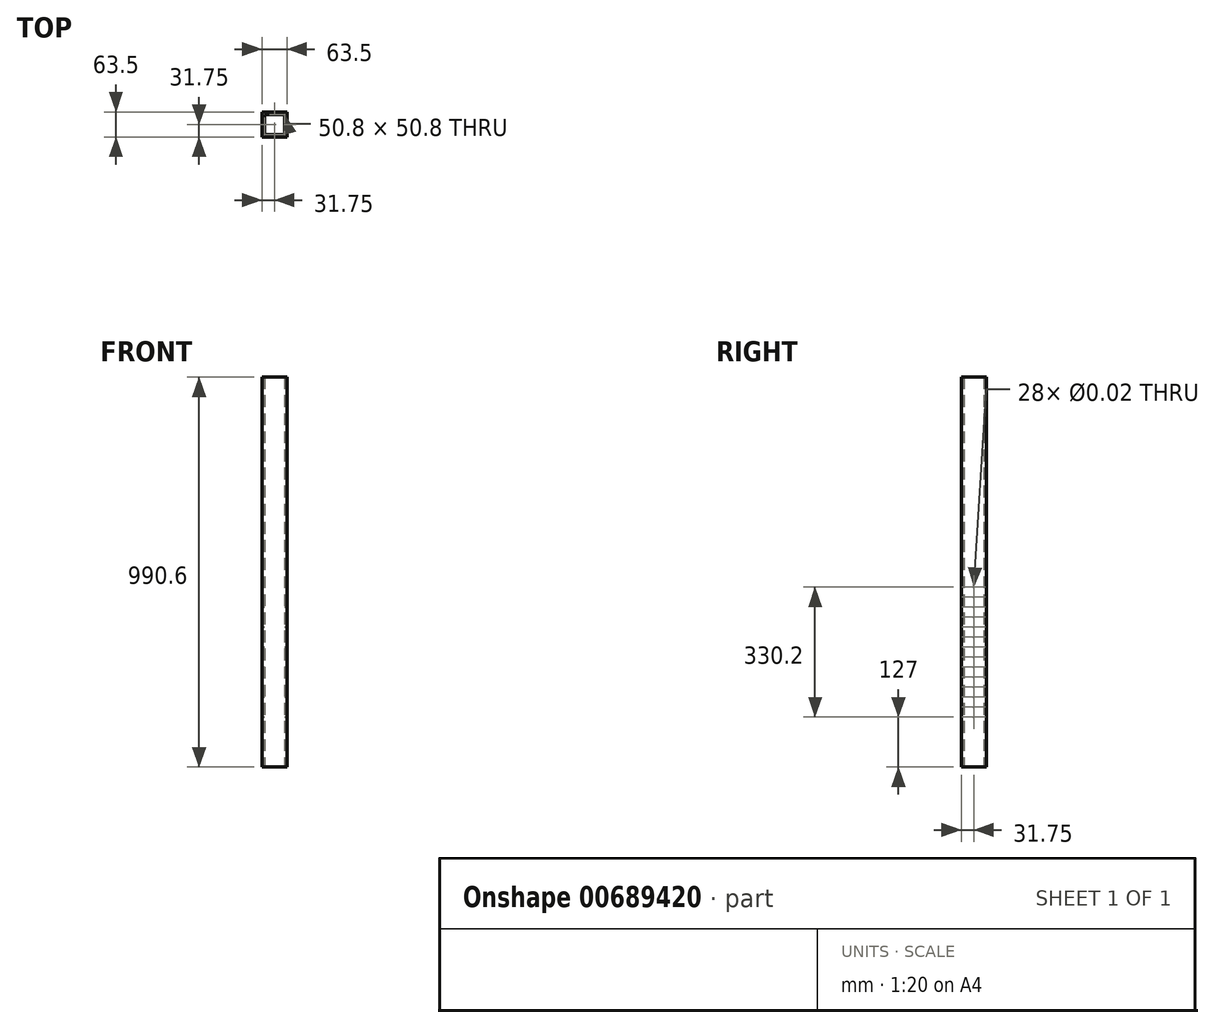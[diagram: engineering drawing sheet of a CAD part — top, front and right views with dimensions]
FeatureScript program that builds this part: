
annotation { "Feature Type Name" : "Feature", "Feature Type Description" : "" }
export const myFeature = defineFeature(function(context is Context, id is Id, definition is map)
    precondition{}
    {
        {
            var Q0;
            Q0=qCreatedBy(makeId("Top.planeOp"),FACE);
            var sketch = newSketch(context, id + "F0", { "sketchPlane" : qUnion([Q0])});
            skLineSegment(sketch, "E0.bottom", {"start": v(-31.75, 31.75) * mm, "end": v(31.75, 31.75) * mm});
            skLineSegment(sketch, "E0.top", {"start": v(-31.75, -31.75) * mm, "end": v(31.75, -31.75) * mm});
            skLineSegment(sketch, "E0.left", {"start": v(-31.75, 31.75) * mm, "end": v(-31.75, -31.75) * mm});
            skLineSegment(sketch, "E0.right", {"start": v(31.75, 31.75) * mm, "end": v(31.75, -31.75) * mm});
            skPoint(sketch, "E0.middle", {"position": v(0, 0) * mm});
            skLineSegment(sketch, "E1.bottom", {"start": v(-25.4, 25.4) * mm, "end": v(25.4, 25.4) * mm});
            skLineSegment(sketch, "E1.top", {"start": v(-25.4, -25.4) * mm, "end": v(25.4, -25.4) * mm});
            skLineSegment(sketch, "E1.left", {"start": v(-25.4, 25.4) * mm, "end": v(-25.4, -25.4) * mm});
            skLineSegment(sketch, "E1.right", {"start": v(25.4, 25.4) * mm, "end": v(25.4, -25.4) * mm});
            skSolve(sketch);
        }
        {
            var Q0;
            Q0=makeQuery(id+"F0.imprint","IMPRINT",FACE,{"disambiguationData":[TD([[makeQuery(id+"F0.imprint","IMPRINT",EDGE,{"derivedFrom":sQuery(id+"F0.wireOp",EDGE,"E0.bottom")}),-1.0]])]});
            extrude(context, id + "F1", {"entities" : qUnion([Q0]), "depth" : 990.6 * mm, "offsetDistance" : 25.4 * mm});
        }
        {
            var Q0;
            Q0=makeQuery(id+"F1.opExtrude","SWEPT_FACE",FACE,{"disambiguationData":[OSD([sQuery(id+"F0.wireOp",EDGE,"E0.right")])]});
            var sketch = newSketch(context, id + "F2", { "sketchPlane" : qUnion([Q0])});
            skPoint(sketch, "E2", {"position": v(0, 127) * mm});
            skPoint(sketch, "E3.0.1.0", {"position": v(0, 152.4) * mm});
            skPoint(sketch, "E3.0.2.0", {"position": v(0, 177.8) * mm});
            skPoint(sketch, "E3.0.3.0", {"position": v(0, 203.2) * mm});
            skPoint(sketch, "E3.0.4.0", {"position": v(0, 228.6) * mm});
            skPoint(sketch, "E3.0.5.0", {"position": v(0, 254) * mm});
            skPoint(sketch, "E3.0.6.0", {"position": v(0, 279.4) * mm});
            skPoint(sketch, "E3.0.7.0", {"position": v(0, 304.8) * mm});
            skPoint(sketch, "E3.0.8.0", {"position": v(0, 330.2) * mm});
            skPoint(sketch, "E3.0.9.0", {"position": v(0, 355.6) * mm});
            skPoint(sketch, "E3.0.10.0", {"position": v(0, 381) * mm});
            skPoint(sketch, "E3.0.11.0", {"position": v(0, 406.4) * mm});
            skPoint(sketch, "E3.0.12.0", {"position": v(0, 431.8) * mm});
            skPoint(sketch, "E3.0.13.0", {"position": v(0, 457.2) * mm});
            skLineSegment(sketch, "E3.direction1", {"start": v(0, 127) * mm, "end": v(25.4, 127) * mm, "construction": true});
            skLineSegment(sketch, "E3.direction2", {"start": v(0, 127) * mm, "end": v(0, 152.4) * mm, "construction": true});
            skSolve(sketch);
        }
        {
            var Q0;
            Q0=sQuery(id+"F2.wireOp",VERTEX,"E2");
            var Q1;
            Q1=sQuery(id+"F2.wireOp",VERTEX,"E3.0.1.0");
            var Q2;
            Q2=sQuery(id+"F2.wireOp",VERTEX,"E3.0.2.0");
            var Q3;
            Q3=sQuery(id+"F2.wireOp",VERTEX,"E3.0.3.0");
            var Q4;
            Q4=sQuery(id+"F2.wireOp",VERTEX,"E3.0.4.0");
            var Q5;
            Q5=sQuery(id+"F2.wireOp",VERTEX,"E3.0.5.0");
            var Q6;
            Q6=sQuery(id+"F2.wireOp",VERTEX,"E3.0.6.0");
            var Q7;
            Q7=sQuery(id+"F2.wireOp",VERTEX,"E3.0.7.0");
            var Q8;
            Q8=sQuery(id+"F2.wireOp",VERTEX,"E3.0.8.0");
            var Q9;
            Q9=sQuery(id+"F2.wireOp",VERTEX,"E3.0.9.0");
            var Q10;
            Q10=sQuery(id+"F2.wireOp",VERTEX,"E3.0.10.0");
            var Q11;
            Q11=sQuery(id+"F2.wireOp",VERTEX,"E3.0.11.0");
            var Q12;
            Q12=sQuery(id+"F2.wireOp",VERTEX,"E3.0.12.0");
            var Q13;
            Q13=sQuery(id+"F2.wireOp",VERTEX,"E3.0.13.0");
            var Q14;
            Q14=makeQuery(id+"F1.opExtrude","SWEPT_BODY",BODY,{"disambiguationData":[OSD([sQuery(id+"F0.wireOp",EDGE,"E0.bottom"),sQuery(id+"F0.wireOp",EDGE,"E0.top"),sQuery(id+"F0.wireOp",EDGE,"E0.left"),sQuery(id+"F0.wireOp",EDGE,"E0.right"),sQuery(id+"F0.wireOp",EDGE,"E1.bottom"),sQuery(id+"F0.wireOp",EDGE,"E1.top"),sQuery(id+"F0.wireOp",EDGE,"E1.left"),sQuery(id+"F0.wireOp",EDGE,"E1.right")])]});
            hole(context, id + "F3", {"style" : HoleStyle.SIMPLE, "endStyle" : HoleEndStyle.THROUGH, "standardTappedOrClearance" : lookupTablePath({ "standard" : "ANSI", "size" : "1/2 (0.5)", "type" : "Drilled" }), "standardBlindInLast" : lookupTablePath({ "standard" : "ANSI", "size" : "1/2", "type" : "Drilled" }), "holeDiameter" : 1 / 50.8 * mm, "majorDiameter" : 6.35 * mm, "tappedDepth" : 10.3 * mm, "tapClearance" : 3, "locations" : qUnion([Q0, Q1, Q2, Q3, Q4, Q5, Q6, Q7, Q8, Q9, Q10, Q11, Q12, Q13]), "scope" : qUnion([Q14])});
        }
    });
